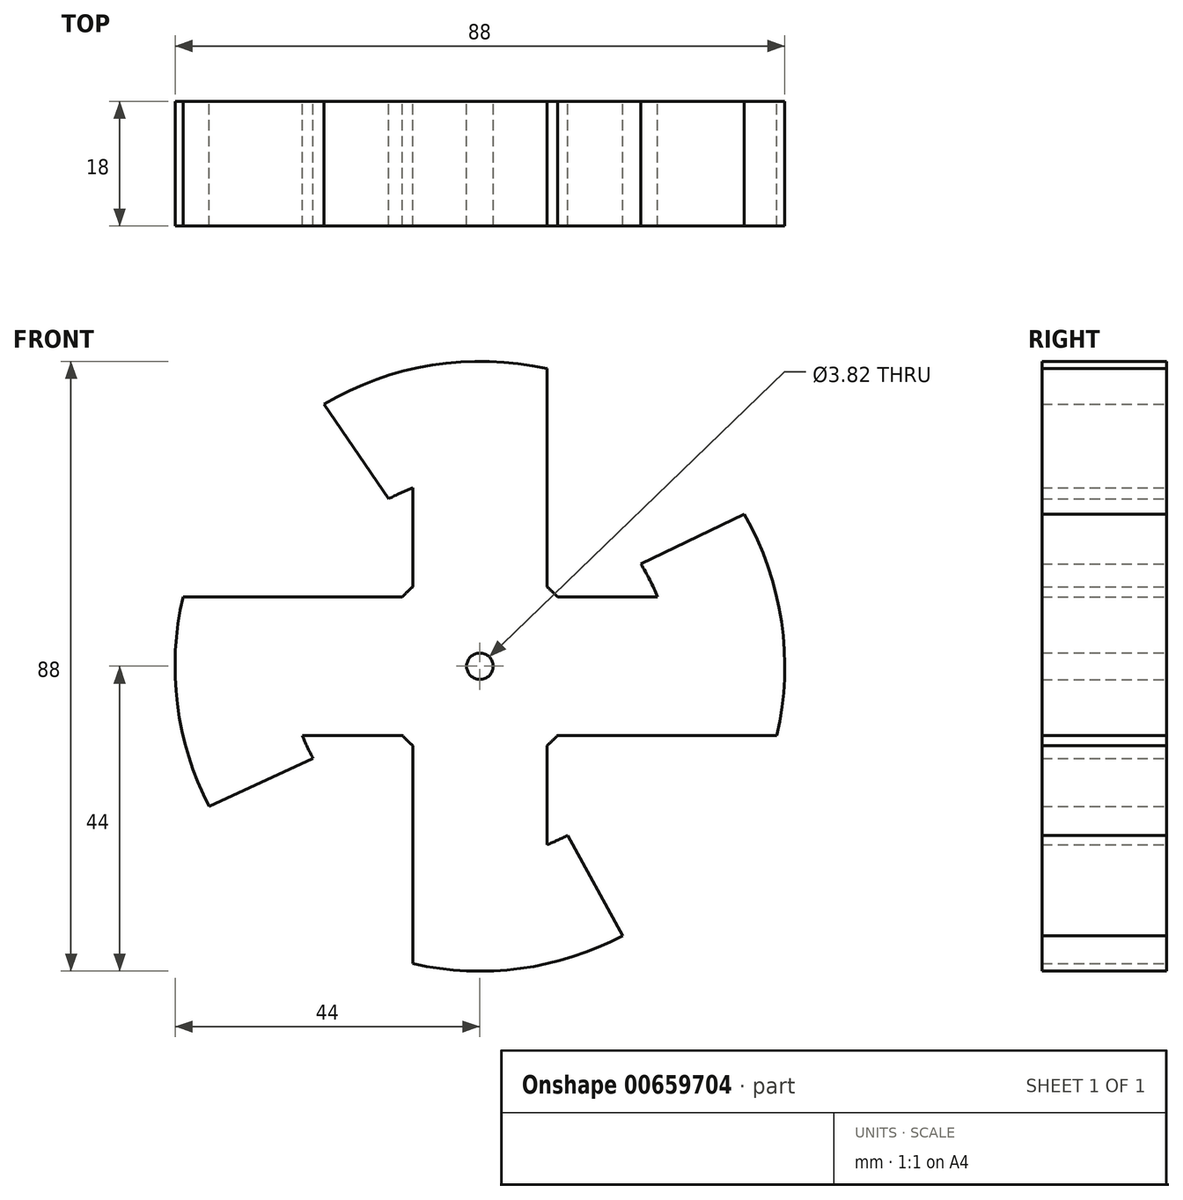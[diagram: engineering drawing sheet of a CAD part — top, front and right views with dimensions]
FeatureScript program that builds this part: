
annotation { "Feature Type Name" : "Feature", "Feature Type Description" : "" }
export const myFeature = defineFeature(function(context is Context, id is Id, definition is map)
    precondition{}
    {
        {
            var Q0;
            Q0=qCreatedBy(makeId("Front.planeOp"),FACE);
            var sketch = newSketch(context, id + "F0", { "sketchPlane" : qUnion([Q0])});
            skArc(sketch, "E0", {"start": v(-9.66, 11.47) * mm, "mid": v(-10.45, 10.76) * mm, "end": v(-11.18, 10) * mm});
            skCircle(sketch, "E1", {"center": v(0, 0) * mm, "radius": 1.9 * mm});
            skCircle(sketch, "E2", {"center": v(0, 0) * mm, "radius": 49 * mm});
            skArc(sketch, "E3", {"start": v(-42.85, 10) * mm, "mid": v(-43.66, -5.46) * mm, "end": v(-39.06, -20.25) * mm});
            skArc(sketch, "E4", {"start": v(-9.66, 25.75) * mm, "mid": v(-11.45, 25) * mm, "end": v(-13.17, 24.14) * mm});
            skLineSegment(sketch, "E5", {"start": v(11.18, 10) * mm, "end": v(25.62, 10) * mm});
            skLineSegment(sketch, "E6", {"start": v(11.18, -10) * mm, "end": v(42.85, -10) * mm});
            skLineSegment(sketch, "E7", {"start": v(-11.18, 10) * mm, "end": v(-42.85, 10) * mm});
            skLineSegment(sketch, "E8", {"start": v(-11.18, -10) * mm, "end": v(-25.62, -10) * mm});
            skLineSegment(sketch, "E9", {"start": v(-9.66, 11.47) * mm, "end": v(-9.66, 25.75) * mm});
            skLineSegment(sketch, "E10", {"start": v(9.66, 11.47) * mm, "end": v(9.66, 42.93) * mm});
            skLineSegment(sketch, "E11", {"start": v(-9.66, -11.47) * mm, "end": v(-9.66, -42.93) * mm});
            skLineSegment(sketch, "E12", {"start": v(9.66, -11.47) * mm, "end": v(9.66, -25.75) * mm});
            skLineSegment(sketch, "E13", {"start": v(-39.06, -20.25) * mm, "end": v(-24.07, -13.3) * mm});
            skLineSegment(sketch, "E14", {"start": v(12.65, -24.42) * mm, "end": v(20.62, -38.87) * mm});
            skLineSegment(sketch, "E15", {"start": v(23.2, 14.77) * mm, "end": v(38.14, 21.94) * mm});
            skLineSegment(sketch, "E16", {"start": v(-13.17, 24.14) * mm, "end": v(-22.5, 37.81) * mm});
            skArc(sketch, "E17.trimOffspring", {"start": v(-25.62, -10) * mm, "mid": v(-24.9, -11.68) * mm, "end": v(-24.07, -13.3) * mm});
            skArc(sketch, "E18.trimOffspring", {"start": v(9.66, 42.93) * mm, "mid": v(-6.9, 43.45) * mm, "end": v(-22.5, 37.81) * mm});
            skArc(sketch, "E19.trimOffspring", {"start": v(25.62, 10) * mm, "mid": v(24.52, 12.44) * mm, "end": v(23.2, 14.77) * mm});
            skPoint(sketch, "E20.orphan", {"position": v(0, 10) * mm});
            skPoint(sketch, "E21.orphan", {"position": v(0, -10) * mm});
            skPoint(sketch, "E22.orphan", {"position": v(-9.66, 0) * mm});
            skArc(sketch, "E23.trimOffspring", {"start": v(9.66, -25.75) * mm, "mid": v(11.18, -25.13) * mm, "end": v(12.65, -24.42) * mm});
            skArc(sketch, "E24.trimOffspring", {"start": v(-9.66, -42.93) * mm, "mid": v(5.84, -43.61) * mm, "end": v(20.62, -38.87) * mm});
            skArc(sketch, "E25.trimOffspring", {"start": v(42.85, -10) * mm, "mid": v(43.53, 6.42) * mm, "end": v(38.14, 21.94) * mm});
            skArc(sketch, "E26.trimOffspring", {"start": v(11.18, 10) * mm, "mid": v(10.45, 10.76) * mm, "end": v(9.66, 11.47) * mm});
            skPoint(sketch, "E27.orphan", {"position": v(9.66, 0) * mm});
            skArc(sketch, "E28.trimOffspring", {"start": v(-11.18, -10) * mm, "mid": v(-10.45, -10.76) * mm, "end": v(-9.66, -11.47) * mm});
            skArc(sketch, "E29.trimOffspring", {"start": v(9.66, -11.47) * mm, "mid": v(10.45, -10.76) * mm, "end": v(11.18, -10) * mm});
            skSolve(sketch);
        }
        {
            var Q0;
            Q0=makeQuery(id+"F0.imprint","IMPRINT",FACE,{"disambiguationData":[TD([[makeQuery(id+"F0.imprint","IMPRINT",EDGE,{"derivedFrom":sQuery(id+"F0.wireOp",EDGE,"E0")}),1.0]])]});
            extrude(context, id + "F1", {"entities" : qUnion([Q0]), "depth" : 18 * mm, "offsetDistance" : 25 * mm});
        }
    });
